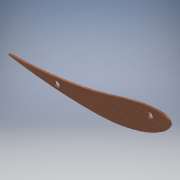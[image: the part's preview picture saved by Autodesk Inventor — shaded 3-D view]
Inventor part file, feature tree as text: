
AUTODESK INVENTOR PART (.ipt)
format: ipt  version: 2018 (Build 220112000, 112)  size: 140,288 bytes
history: native  units: mm
features: extrude x2, sketch x2, other x1, projected_geometry x1
ambient origin geometry x8: Origin, YZ Plane, XZ Plane, XY Plane, X Axis, Y Axis, Z Axis, Center Point
bodies: Body1 (feature_tree)
feature tree (6):
  extrude  "押し出し1"  Depth=4.0mm TaperAngle=0.0deg
  extrude  "押し出し2"  Depth=290.0mm
  other  "厚み1"
  sketch  "スケッチ1"
  projected_geometry  "投影ループ1"
  sketch  "スケッチ2"
